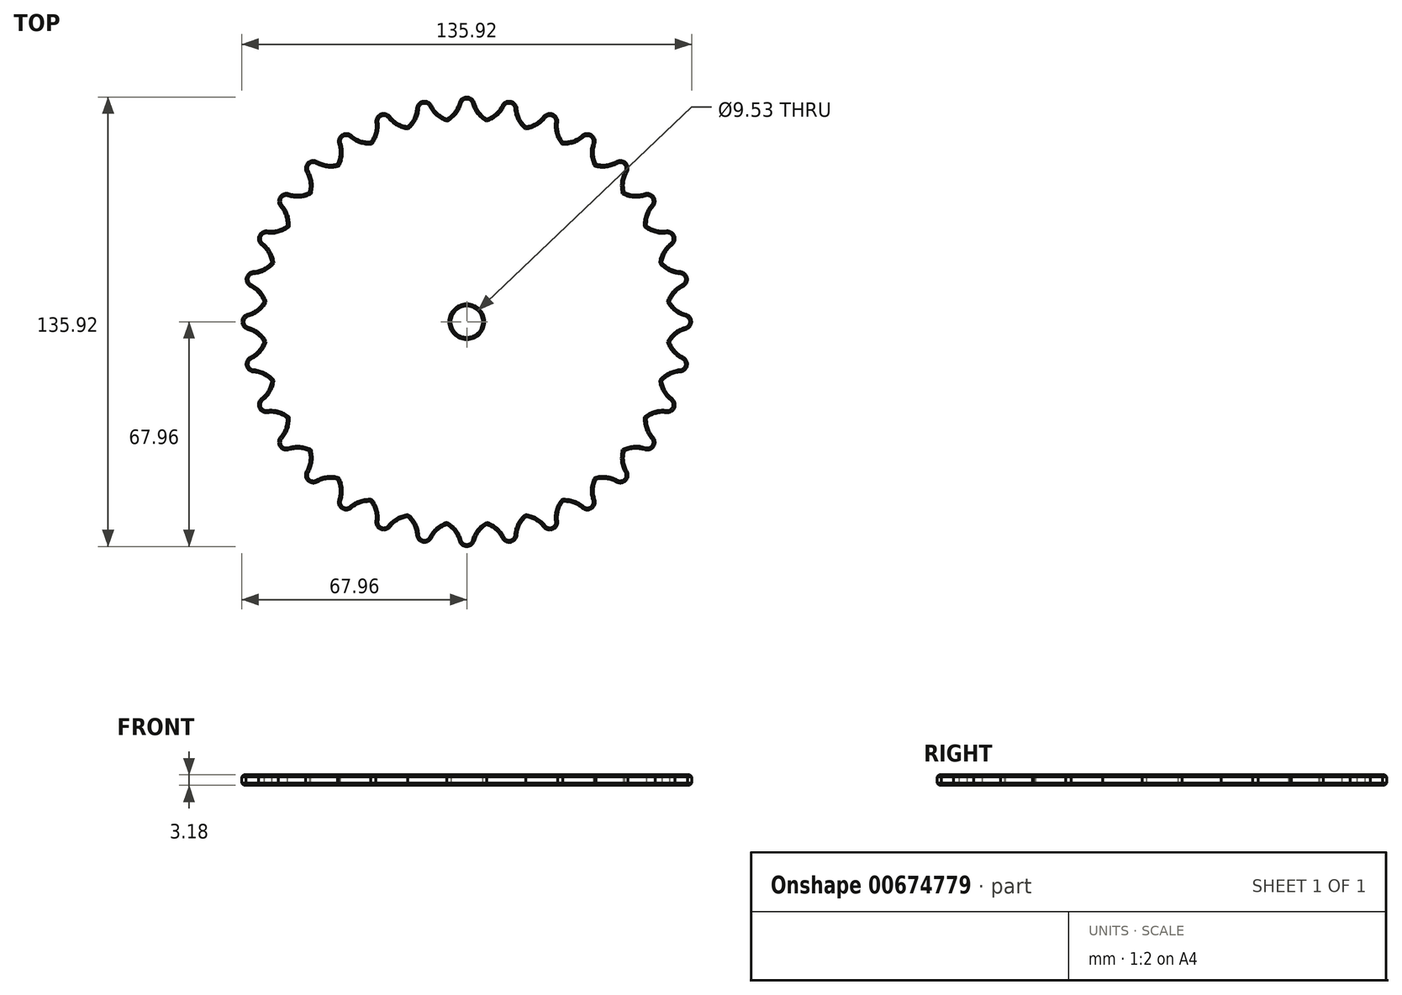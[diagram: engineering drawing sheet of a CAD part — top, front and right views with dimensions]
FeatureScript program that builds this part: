
annotation { "Feature Type Name" : "Feature", "Feature Type Description" : "" }
export const myFeature = defineFeature(function(context is Context, id is Id, definition is map)
    precondition{}
    {
        {
            var Q0;
            Q0=qCreatedBy(makeId("Top.planeOp"),FACE);
            var sketch = newSketch(context, id + "F0", { "sketchPlane" : qUnion([Q0])});
            skCircle(sketch, "E0", {"center": v(0, 0) * mm, "radius": 64.79 * mm, "construction": true});
            skCircle(sketch, "E1.0", {"center": v(0, 0) * mm, "radius": 67.96 * mm});
            skCircle(sketch, "E2.0", {"center": v(0, 0) * mm, "radius": 61.61 * mm, "construction": true});
            skCircle(sketch, "E3", {"center": v(0, 0) * mm, "radius": 4.76 * mm});
            skLineSegment(sketch, "E4", {"start": v(0, 0) * mm, "end": v(0, 67.96) * mm});
            skLineSegment(sketch, "E5", {"start": v(0, 0) * mm, "end": v(6.04, 61.31) * mm});
            skCircle(sketch, "E6", {"center": v(0, 67.96) * mm, "radius": 2.38 * mm});
            skLineSegment(sketch, "E7", {"start": v(0, 67.96) * mm, "end": v(2.94, 69.66) * mm});
            skLineSegment(sketch, "E8", {"start": v(0, 67.96) * mm, "end": v(2.38, 67.96) * mm});
            skArc(sketch, "E9", {"start": v(2.3, 66.2) * mm, "mid": v(0, 67.96) * mm, "end": v(-2.3, 66.2) * mm});
            skLineSegment(sketch, "E10", {"start": v(0, 65.58) * mm, "end": v(2.38, 65.58) * mm});
            skLineSegment(sketch, "E11", {"start": v(0, 65.58) * mm, "end": v(3.51, 66.52) * mm});
            skLineSegment(sketch, "E12.MirrorCS", {"start": v(0, 65.58) * mm, "end": v(-3.51, 66.52) * mm});
            skLineSegment(sketch, "E13", {"start": v(2.3, 66.2) * mm, "end": v(2.97, 63.7) * mm});
            skLineSegment(sketch, "E14", {"start": v(-2.3, 66.2) * mm, "end": v(-3.02, 63.53) * mm});
            skArc(sketch, "E15.1.0", {"start": v(-10.66, 65.37) * mm, "mid": v(-13.26, 66.66) * mm, "end": v(-15.17, 64.48) * mm});
            skArc(sketch, "E15.2.0", {"start": v(-23.2, 62.04) * mm, "mid": v(-26, 62.79) * mm, "end": v(-27.46, 60.28) * mm});
            skArc(sketch, "E15.3.0", {"start": v(-34.86, 56.32) * mm, "mid": v(-37.76, 56.5) * mm, "end": v(-38.69, 53.76) * mm});
            skArc(sketch, "E15.4.0", {"start": v(-45.18, 48.43) * mm, "mid": v(-48.06, 48.06) * mm, "end": v(-48.43, 45.18) * mm});
            skArc(sketch, "E15.5.0", {"start": v(-53.76, 38.69) * mm, "mid": v(-56.5, 37.76) * mm, "end": v(-56.32, 34.86) * mm});
            skArc(sketch, "E15.6.0", {"start": v(-60.28, 27.46) * mm, "mid": v(-62.79, 26) * mm, "end": v(-62.04, 23.2) * mm});
            skArc(sketch, "E15.7.0", {"start": v(-64.48, 15.17) * mm, "mid": v(-66.66, 13.26) * mm, "end": v(-65.37, 10.66) * mm});
            skArc(sketch, "E15.8.0", {"start": v(-66.2, 2.3) * mm, "mid": v(-67.96, 0) * mm, "end": v(-66.2, -2.3) * mm});
            skArc(sketch, "E15.9.0", {"start": v(-65.37, -10.66) * mm, "mid": v(-66.66, -13.26) * mm, "end": v(-64.48, -15.17) * mm});
            skArc(sketch, "E15.10.0", {"start": v(-62.04, -23.2) * mm, "mid": v(-62.79, -26) * mm, "end": v(-60.28, -27.46) * mm});
            skArc(sketch, "E15.11.0", {"start": v(-56.32, -34.86) * mm, "mid": v(-56.5, -37.76) * mm, "end": v(-53.76, -38.69) * mm});
            skArc(sketch, "E15.12.0", {"start": v(-48.43, -45.18) * mm, "mid": v(-48.06, -48.06) * mm, "end": v(-45.18, -48.43) * mm});
            skArc(sketch, "E15.13.0", {"start": v(-38.69, -53.76) * mm, "mid": v(-37.76, -56.5) * mm, "end": v(-34.86, -56.32) * mm});
            skArc(sketch, "E15.14.0", {"start": v(-27.46, -60.28) * mm, "mid": v(-26, -62.79) * mm, "end": v(-23.2, -62.04) * mm});
            skArc(sketch, "E15.15.0", {"start": v(-15.17, -64.48) * mm, "mid": v(-13.26, -66.66) * mm, "end": v(-10.66, -65.37) * mm});
            skArc(sketch, "E15.16.0", {"start": v(-2.3, -66.2) * mm, "mid": v(0, -67.96) * mm, "end": v(2.3, -66.2) * mm});
            skArc(sketch, "E15.17.0", {"start": v(10.66, -65.37) * mm, "mid": v(13.26, -66.66) * mm, "end": v(15.17, -64.48) * mm});
            skArc(sketch, "E15.18.0", {"start": v(23.2, -62.04) * mm, "mid": v(26, -62.79) * mm, "end": v(27.46, -60.28) * mm});
            skArc(sketch, "E15.19.0", {"start": v(34.86, -56.32) * mm, "mid": v(37.76, -56.5) * mm, "end": v(38.69, -53.76) * mm});
            skArc(sketch, "E15.20.0", {"start": v(45.18, -48.43) * mm, "mid": v(48.06, -48.06) * mm, "end": v(48.43, -45.18) * mm});
            skArc(sketch, "E15.21.0", {"start": v(53.76, -38.69) * mm, "mid": v(56.5, -37.76) * mm, "end": v(56.32, -34.86) * mm});
            skArc(sketch, "E15.22.0", {"start": v(60.28, -27.46) * mm, "mid": v(62.79, -26) * mm, "end": v(62.04, -23.2) * mm});
            skArc(sketch, "E15.23.0", {"start": v(64.48, -15.17) * mm, "mid": v(66.66, -13.26) * mm, "end": v(65.37, -10.66) * mm});
            skArc(sketch, "E15.24.0", {"start": v(66.2, -2.3) * mm, "mid": v(67.96, 0) * mm, "end": v(66.2, 2.3) * mm});
            skArc(sketch, "E15.25.0", {"start": v(65.37, 10.66) * mm, "mid": v(66.66, 13.26) * mm, "end": v(64.48, 15.17) * mm});
            skArc(sketch, "E15.26.0", {"start": v(62.04, 23.2) * mm, "mid": v(62.79, 26) * mm, "end": v(60.28, 27.46) * mm});
            skArc(sketch, "E15.27.0", {"start": v(56.32, 34.86) * mm, "mid": v(56.5, 37.76) * mm, "end": v(53.76, 38.69) * mm});
            skArc(sketch, "E15.28.0", {"start": v(48.43, 45.18) * mm, "mid": v(48.06, 48.06) * mm, "end": v(45.18, 48.43) * mm});
            skArc(sketch, "E15.29.0", {"start": v(38.69, 53.76) * mm, "mid": v(37.76, 56.5) * mm, "end": v(34.86, 56.32) * mm});
            skArc(sketch, "E15.30.0", {"start": v(27.46, 60.28) * mm, "mid": v(26, 62.79) * mm, "end": v(23.2, 62.04) * mm});
            skArc(sketch, "E15.31.0", {"start": v(15.17, 64.48) * mm, "mid": v(13.26, 66.66) * mm, "end": v(10.66, 65.37) * mm});
            skArc(sketch, "E16", {"start": v(2.3, 66.2) * mm, "mid": v(3.69, 63.38) * mm, "end": v(6.04, 61.31) * mm});
            skLineSegment(sketch, "E17.MirrorCS", {"start": v(0, 0) * mm, "end": v(-6.04, 61.31) * mm});
            skArc(sketch, "E18", {"start": v(-6.04, 61.31) * mm, "mid": v(-3.69, 63.38) * mm, "end": v(-2.3, 66.2) * mm});
            skArc(sketch, "E19.1.0", {"start": v(-10.66, 65.37) * mm, "mid": v(-8.75, 62.89) * mm, "end": v(-6.04, 61.31) * mm});
            skArc(sketch, "E19.1.1", {"start": v(-17.88, 58.96) * mm, "mid": v(-15.98, 61.45) * mm, "end": v(-15.17, 64.48) * mm});
            skArc(sketch, "E19.2.0", {"start": v(-23.2, 62.04) * mm, "mid": v(-20.85, 59.97) * mm, "end": v(-17.88, 58.96) * mm});
            skArc(sketch, "E19.2.1", {"start": v(-29.04, 54.34) * mm, "mid": v(-27.66, 57.15) * mm, "end": v(-27.46, 60.28) * mm});
            skArc(sketch, "E19.3.0", {"start": v(-34.86, 56.32) * mm, "mid": v(-32.15, 54.75) * mm, "end": v(-29.04, 54.34) * mm});
            skArc(sketch, "E19.3.1", {"start": v(-39.09, 47.63) * mm, "mid": v(-38.28, 50.65) * mm, "end": v(-38.69, 53.76) * mm});
            skArc(sketch, "E19.4.0", {"start": v(-45.18, 48.43) * mm, "mid": v(-42.21, 47.43) * mm, "end": v(-39.09, 47.63) * mm});
            skArc(sketch, "E19.4.1", {"start": v(-47.63, 39.09) * mm, "mid": v(-47.43, 42.21) * mm, "end": v(-48.43, 45.18) * mm});
            skArc(sketch, "E19.5.0", {"start": v(-53.76, 38.69) * mm, "mid": v(-50.65, 38.28) * mm, "end": v(-47.63, 39.09) * mm});
            skArc(sketch, "E19.5.1", {"start": v(-54.34, 29.04) * mm, "mid": v(-54.75, 32.15) * mm, "end": v(-56.32, 34.86) * mm});
            skArc(sketch, "E19.6.0", {"start": v(-60.28, 27.46) * mm, "mid": v(-57.15, 27.66) * mm, "end": v(-54.34, 29.04) * mm});
            skArc(sketch, "E19.6.1", {"start": v(-58.96, 17.88) * mm, "mid": v(-59.97, 20.85) * mm, "end": v(-62.04, 23.2) * mm});
            skArc(sketch, "E19.7.0", {"start": v(-64.48, 15.17) * mm, "mid": v(-61.45, 15.98) * mm, "end": v(-58.96, 17.88) * mm});
            skArc(sketch, "E19.7.1", {"start": v(-61.31, 6.04) * mm, "mid": v(-62.89, 8.75) * mm, "end": v(-65.37, 10.66) * mm});
            skArc(sketch, "E19.8.0", {"start": v(-66.2, 2.3) * mm, "mid": v(-63.38, 3.69) * mm, "end": v(-61.31, 6.04) * mm});
            skArc(sketch, "E19.8.1", {"start": v(-61.31, -6.04) * mm, "mid": v(-63.38, -3.69) * mm, "end": v(-66.2, -2.3) * mm});
            skArc(sketch, "E19.9.0", {"start": v(-65.37, -10.66) * mm, "mid": v(-62.89, -8.75) * mm, "end": v(-61.31, -6.04) * mm});
            skArc(sketch, "E19.9.1", {"start": v(-58.96, -17.88) * mm, "mid": v(-61.45, -15.98) * mm, "end": v(-64.48, -15.17) * mm});
            skArc(sketch, "E19.10.0", {"start": v(-62.04, -23.2) * mm, "mid": v(-59.97, -20.85) * mm, "end": v(-58.96, -17.88) * mm});
            skArc(sketch, "E19.10.1", {"start": v(-54.34, -29.04) * mm, "mid": v(-57.15, -27.66) * mm, "end": v(-60.28, -27.46) * mm});
            skArc(sketch, "E19.11.0", {"start": v(-56.32, -34.86) * mm, "mid": v(-54.75, -32.15) * mm, "end": v(-54.34, -29.04) * mm});
            skArc(sketch, "E19.11.1", {"start": v(-47.63, -39.09) * mm, "mid": v(-50.65, -38.28) * mm, "end": v(-53.76, -38.69) * mm});
            skArc(sketch, "E19.12.0", {"start": v(-48.43, -45.18) * mm, "mid": v(-47.43, -42.21) * mm, "end": v(-47.63, -39.09) * mm});
            skArc(sketch, "E19.12.1", {"start": v(-39.09, -47.63) * mm, "mid": v(-42.21, -47.43) * mm, "end": v(-45.18, -48.43) * mm});
            skArc(sketch, "E19.13.0", {"start": v(-38.69, -53.76) * mm, "mid": v(-38.28, -50.65) * mm, "end": v(-39.09, -47.63) * mm});
            skArc(sketch, "E19.13.1", {"start": v(-29.04, -54.34) * mm, "mid": v(-32.15, -54.75) * mm, "end": v(-34.86, -56.32) * mm});
            skArc(sketch, "E19.14.0", {"start": v(-27.46, -60.28) * mm, "mid": v(-27.66, -57.15) * mm, "end": v(-29.04, -54.34) * mm});
            skArc(sketch, "E19.14.1", {"start": v(-17.88, -58.96) * mm, "mid": v(-20.85, -59.97) * mm, "end": v(-23.2, -62.04) * mm});
            skArc(sketch, "E19.15.0", {"start": v(-15.17, -64.48) * mm, "mid": v(-15.98, -61.45) * mm, "end": v(-17.88, -58.96) * mm});
            skArc(sketch, "E19.15.1", {"start": v(-6.04, -61.31) * mm, "mid": v(-8.75, -62.89) * mm, "end": v(-10.66, -65.37) * mm});
            skArc(sketch, "E19.16.0", {"start": v(-2.3, -66.2) * mm, "mid": v(-3.69, -63.38) * mm, "end": v(-6.04, -61.31) * mm});
            skArc(sketch, "E19.16.1", {"start": v(6.04, -61.31) * mm, "mid": v(3.69, -63.38) * mm, "end": v(2.3, -66.2) * mm});
            skArc(sketch, "E19.17.0", {"start": v(10.66, -65.37) * mm, "mid": v(8.75, -62.89) * mm, "end": v(6.04, -61.31) * mm});
            skArc(sketch, "E19.17.1", {"start": v(17.88, -58.96) * mm, "mid": v(15.98, -61.45) * mm, "end": v(15.17, -64.48) * mm});
            skArc(sketch, "E19.18.0", {"start": v(23.2, -62.04) * mm, "mid": v(20.85, -59.97) * mm, "end": v(17.88, -58.96) * mm});
            skArc(sketch, "E19.18.1", {"start": v(29.04, -54.34) * mm, "mid": v(27.66, -57.15) * mm, "end": v(27.46, -60.28) * mm});
            skArc(sketch, "E19.19.0", {"start": v(34.86, -56.32) * mm, "mid": v(32.15, -54.75) * mm, "end": v(29.04, -54.34) * mm});
            skArc(sketch, "E19.19.1", {"start": v(39.09, -47.63) * mm, "mid": v(38.28, -50.65) * mm, "end": v(38.69, -53.76) * mm});
            skArc(sketch, "E19.20.0", {"start": v(45.18, -48.43) * mm, "mid": v(42.21, -47.43) * mm, "end": v(39.09, -47.63) * mm});
            skArc(sketch, "E19.20.1", {"start": v(47.63, -39.09) * mm, "mid": v(47.43, -42.21) * mm, "end": v(48.43, -45.18) * mm});
            skArc(sketch, "E19.21.0", {"start": v(53.76, -38.69) * mm, "mid": v(50.65, -38.28) * mm, "end": v(47.63, -39.09) * mm});
            skArc(sketch, "E19.21.1", {"start": v(54.34, -29.04) * mm, "mid": v(54.75, -32.15) * mm, "end": v(56.32, -34.86) * mm});
            skArc(sketch, "E19.22.0", {"start": v(60.28, -27.46) * mm, "mid": v(57.15, -27.66) * mm, "end": v(54.34, -29.04) * mm});
            skArc(sketch, "E19.22.1", {"start": v(58.96, -17.88) * mm, "mid": v(59.97, -20.85) * mm, "end": v(62.04, -23.2) * mm});
            skArc(sketch, "E19.23.0", {"start": v(64.48, -15.17) * mm, "mid": v(61.45, -15.98) * mm, "end": v(58.96, -17.88) * mm});
            skArc(sketch, "E19.23.1", {"start": v(61.31, -6.04) * mm, "mid": v(62.89, -8.75) * mm, "end": v(65.37, -10.66) * mm});
            skArc(sketch, "E19.24.0", {"start": v(66.2, -2.3) * mm, "mid": v(63.38, -3.69) * mm, "end": v(61.31, -6.04) * mm});
            skArc(sketch, "E19.24.1", {"start": v(61.31, 6.04) * mm, "mid": v(63.38, 3.69) * mm, "end": v(66.2, 2.3) * mm});
            skArc(sketch, "E19.25.0", {"start": v(65.37, 10.66) * mm, "mid": v(62.89, 8.75) * mm, "end": v(61.31, 6.04) * mm});
            skArc(sketch, "E19.25.1", {"start": v(58.96, 17.88) * mm, "mid": v(61.45, 15.98) * mm, "end": v(64.48, 15.17) * mm});
            skArc(sketch, "E19.26.0", {"start": v(62.04, 23.2) * mm, "mid": v(59.97, 20.85) * mm, "end": v(58.96, 17.88) * mm});
            skArc(sketch, "E19.26.1", {"start": v(54.34, 29.04) * mm, "mid": v(57.15, 27.66) * mm, "end": v(60.28, 27.46) * mm});
            skArc(sketch, "E19.27.0", {"start": v(56.32, 34.86) * mm, "mid": v(54.75, 32.15) * mm, "end": v(54.34, 29.04) * mm});
            skArc(sketch, "E19.27.1", {"start": v(47.63, 39.09) * mm, "mid": v(50.65, 38.28) * mm, "end": v(53.76, 38.69) * mm});
            skArc(sketch, "E19.28.0", {"start": v(48.43, 45.18) * mm, "mid": v(47.43, 42.21) * mm, "end": v(47.63, 39.09) * mm});
            skArc(sketch, "E19.28.1", {"start": v(39.09, 47.63) * mm, "mid": v(42.21, 47.43) * mm, "end": v(45.18, 48.43) * mm});
            skArc(sketch, "E19.29.0", {"start": v(38.69, 53.76) * mm, "mid": v(38.28, 50.65) * mm, "end": v(39.09, 47.63) * mm});
            skArc(sketch, "E19.29.1", {"start": v(29.04, 54.34) * mm, "mid": v(32.15, 54.75) * mm, "end": v(34.86, 56.32) * mm});
            skArc(sketch, "E19.30.0", {"start": v(27.46, 60.28) * mm, "mid": v(27.66, 57.15) * mm, "end": v(29.04, 54.34) * mm});
            skArc(sketch, "E19.30.1", {"start": v(17.88, 58.96) * mm, "mid": v(20.85, 59.97) * mm, "end": v(23.2, 62.04) * mm});
            skArc(sketch, "E19.31.0", {"start": v(15.17, 64.48) * mm, "mid": v(15.98, 61.45) * mm, "end": v(17.88, 58.96) * mm});
            skArc(sketch, "E19.31.1", {"start": v(6.04, 61.31) * mm, "mid": v(8.75, 62.89) * mm, "end": v(10.66, 65.37) * mm});
            skPoint(sketch, "E20", {"position": v(-27.4, 58.7) * mm});
            skPoint(sketch, "E21", {"position": v(-15.43, 62.92) * mm});
            skSolve(sketch);
        }
        {
            var Q0;
            {var subQ28=sQuery(id+"F0.wireOp",EDGE,"E19.1.0");Q0=makeQuery(id+"F0.imprint","IMPRINT",FACE,{"disambiguationData":[TD([[makeQuery(id+"F0.imprint","IMPRINT",EDGE,{"derivedFrom":subQ28}),-1.0]])]});}
            var Q1;
            {var subQ5=sQuery(id+"F0.wireOp",EDGE,"E16");Q1=makeQuery(id+"F0.imprint","IMPRINT",FACE,{"disambiguationData":[TD([[makeQuery(id+"F0.imprint","IMPRINT",EDGE,{"derivedFrom":subQ5}),-1.0]])]});}
            var Q2;
            {var subQ9=sQuery(id+"F0.wireOp",EDGE,"E18");Q2=makeQuery(id+"F0.imprint","IMPRINT",FACE,{"disambiguationData":[TD([[makeQuery(id+"F0.imprint","IMPRINT",EDGE,{"derivedFrom":subQ9}),-1.0]])]});}
            var Q3;
            {var subQ3=sQuery(id+"F0.wireOp",EDGE,"E11");var subQ4=sQuery(id+"F0.wireOp",EDGE,"E6");var subQ7=makeQuery(id+"F0.imprint","INTERSECT",VERTEX,{"derivedFrom":[subQ4,subQ3]});Q3=makeQuery(id+"F0.imprint","IMPRINT",FACE,{"disambiguationData":[TD([[makeQuery(id+"F0.imprint","IMPRINT",EDGE,{"disambiguationData":[TD([[subQ7,-1.0]])],"derivedFrom":subQ4}),1.0]])]});}
            var Q4;
            {var subQ0=sQuery(id+"F0.wireOp",EDGE,"E11");var subQ1=sQuery(id+"F0.wireOp",EDGE,"E6");var subQ2=makeQuery(id+"F0.imprint","INTERSECT",VERTEX,{"derivedFrom":[subQ1,subQ0]});Q4=makeQuery(id+"F0.imprint","IMPRINT",FACE,{"disambiguationData":[TD([[makeQuery(id+"F0.imprint","IMPRINT",EDGE,{"disambiguationData":[TD([[subQ2,-1.0]])],"derivedFrom":subQ1}),-1.0]])]});}
            var Q5;
            {var subQ0=sQuery(id+"F0.wireOp",EDGE,"E11");var subQ1=sQuery(id+"F0.wireOp",EDGE,"E6");var subQ3=makeQuery(id+"F0.imprint","INTERSECT",VERTEX,{"derivedFrom":[subQ1,subQ0]});Q5=makeQuery(id+"F0.imprint","IMPRINT",FACE,{"disambiguationData":[TD([[makeQuery(id+"F0.imprint","IMPRINT",EDGE,{"disambiguationData":[TD([[subQ3,1.0]])],"derivedFrom":subQ1}),1.0]])]});}
            var Q6;
            {var subQ0=sQuery(id+"F0.wireOp",EDGE,"E12.MirrorCS");var subQ1=sQuery(id+"F0.wireOp",EDGE,"E6");var subQ3=makeQuery(id+"F0.imprint","INTERSECT",VERTEX,{"derivedFrom":[subQ1,subQ0]});Q6=makeQuery(id+"F0.imprint","IMPRINT",FACE,{"disambiguationData":[TD([[makeQuery(id+"F0.imprint","IMPRINT",EDGE,{"disambiguationData":[TD([[subQ3,-1.0]])],"derivedFrom":subQ1}),1.0]])]});}
            var Q7;
            {var subQ0=sQuery(id+"F0.wireOp",EDGE,"E9");var subQ4=sQuery(id+"F0.wireOp",EDGE,"E6");var subQ7=makeQuery(id+"F0.imprint","INTERSECT",VERTEX,{"disambiguationData":[OD(0.0)],"derivedFrom":[subQ4,subQ0]});Q7=makeQuery(id+"F0.imprint","IMPRINT",FACE,{"disambiguationData":[TD([[makeQuery(id+"F0.imprint","IMPRINT",EDGE,{"disambiguationData":[TD([[subQ7,-1.0]])],"derivedFrom":subQ4}),1.0]])]});}
            var Q8;
            {var subQ0=sQuery(id+"F0.wireOp",EDGE,"E9");var subQ1=sQuery(id+"F0.wireOp",EDGE,"E6");var subQ2=makeQuery(id+"F0.imprint","INTERSECT",VERTEX,{"disambiguationData":[OD(0.0)],"derivedFrom":[subQ1,subQ0]});Q8=makeQuery(id+"F0.imprint","IMPRINT",FACE,{"disambiguationData":[TD([[makeQuery(id+"F0.imprint","IMPRINT",EDGE,{"disambiguationData":[TD([[subQ2,-1.0]])],"derivedFrom":subQ1}),-1.0]])]});}
            extrude(context, id + "F1", {"entities" : qUnion([Q0, Q1, Q2, Q3, Q4, Q5, Q6, Q7, Q8]), "depth" : 3.17 * mm, "offsetDistance" : 25.4 * mm});
        }
        {
            var Q0;
            Q0=makeQuery(id+"F1.opExtrude","CAP_FACE",FACE,{"disambiguationData":[OSD([sQuery(id+"F0.wireOp",EDGE,"E3"),sQuery(id+"F0.wireOp",EDGE,"E9"),sQuery(id+"F0.wireOp",EDGE,"E15.1.0"),sQuery(id+"F0.wireOp",EDGE,"E15.2.0"),sQuery(id+"F0.wireOp",EDGE,"E15.3.0"),sQuery(id+"F0.wireOp",EDGE,"E15.4.0"),sQuery(id+"F0.wireOp",EDGE,"E15.5.0"),sQuery(id+"F0.wireOp",EDGE,"E15.6.0"),sQuery(id+"F0.wireOp",EDGE,"E15.7.0"),sQuery(id+"F0.wireOp",EDGE,"E15.8.0"),sQuery(id+"F0.wireOp",EDGE,"E15.9.0"),sQuery(id+"F0.wireOp",EDGE,"E15.10.0"),sQuery(id+"F0.wireOp",EDGE,"E15.11.0"),sQuery(id+"F0.wireOp",EDGE,"E15.12.0"),sQuery(id+"F0.wireOp",EDGE,"E15.13.0"),sQuery(id+"F0.wireOp",EDGE,"E15.14.0"),sQuery(id+"F0.wireOp",EDGE,"E15.15.0"),sQuery(id+"F0.wireOp",EDGE,"E15.16.0"),sQuery(id+"F0.wireOp",EDGE,"E15.17.0"),sQuery(id+"F0.wireOp",EDGE,"E15.18.0"),sQuery(id+"F0.wireOp",EDGE,"E15.19.0"),sQuery(id+"F0.wireOp",EDGE,"E15.20.0"),sQuery(id+"F0.wireOp",EDGE,"E15.21.0"),sQuery(id+"F0.wireOp",EDGE,"E15.22.0"),sQuery(id+"F0.wireOp",EDGE,"E15.23.0"),sQuery(id+"F0.wireOp",EDGE,"E15.24.0"),sQuery(id+"F0.wireOp",EDGE,"E15.25.0"),sQuery(id+"F0.wireOp",EDGE,"E15.26.0"),sQuery(id+"F0.wireOp",EDGE,"E15.27.0"),sQuery(id+"F0.wireOp",EDGE,"E15.28.0"),sQuery(id+"F0.wireOp",EDGE,"E15.29.0"),sQuery(id+"F0.wireOp",EDGE,"E15.30.0"),sQuery(id+"F0.wireOp",EDGE,"E15.31.0"),sQuery(id+"F0.wireOp",EDGE,"E16"),sQuery(id+"F0.wireOp",EDGE,"E18"),sQuery(id+"F0.wireOp",EDGE,"E19.1.0"),sQuery(id+"F0.wireOp",EDGE,"E19.1.1"),sQuery(id+"F0.wireOp",EDGE,"E19.2.0"),sQuery(id+"F0.wireOp",EDGE,"E19.2.1"),sQuery(id+"F0.wireOp",EDGE,"E19.3.0"),sQuery(id+"F0.wireOp",EDGE,"E19.3.1"),sQuery(id+"F0.wireOp",EDGE,"E19.4.0"),sQuery(id+"F0.wireOp",EDGE,"E19.4.1"),sQuery(id+"F0.wireOp",EDGE,"E19.5.0"),sQuery(id+"F0.wireOp",EDGE,"E19.5.1"),sQuery(id+"F0.wireOp",EDGE,"E19.6.0"),sQuery(id+"F0.wireOp",EDGE,"E19.6.1"),sQuery(id+"F0.wireOp",EDGE,"E19.7.0"),sQuery(id+"F0.wireOp",EDGE,"E19.7.1"),sQuery(id+"F0.wireOp",EDGE,"E19.8.0"),sQuery(id+"F0.wireOp",EDGE,"E19.8.1"),sQuery(id+"F0.wireOp",EDGE,"E19.9.0"),sQuery(id+"F0.wireOp",EDGE,"E19.9.1"),sQuery(id+"F0.wireOp",EDGE,"E19.10.0"),sQuery(id+"F0.wireOp",EDGE,"E19.10.1"),sQuery(id+"F0.wireOp",EDGE,"E19.11.0"),sQuery(id+"F0.wireOp",EDGE,"E19.11.1"),sQuery(id+"F0.wireOp",EDGE,"E19.12.0"),sQuery(id+"F0.wireOp",EDGE,"E19.12.1"),sQuery(id+"F0.wireOp",EDGE,"E19.13.0"),sQuery(id+"F0.wireOp",EDGE,"E19.13.1"),sQuery(id+"F0.wireOp",EDGE,"E19.14.0"),sQuery(id+"F0.wireOp",EDGE,"E19.14.1"),sQuery(id+"F0.wireOp",EDGE,"E19.15.0"),sQuery(id+"F0.wireOp",EDGE,"E19.15.1"),sQuery(id+"F0.wireOp",EDGE,"E19.16.0"),sQuery(id+"F0.wireOp",EDGE,"E19.16.1"),sQuery(id+"F0.wireOp",EDGE,"E19.17.0"),sQuery(id+"F0.wireOp",EDGE,"E19.17.1"),sQuery(id+"F0.wireOp",EDGE,"E19.18.0"),sQuery(id+"F0.wireOp",EDGE,"E19.18.1"),sQuery(id+"F0.wireOp",EDGE,"E19.19.0"),sQuery(id+"F0.wireOp",EDGE,"E19.19.1"),sQuery(id+"F0.wireOp",EDGE,"E19.20.0"),sQuery(id+"F0.wireOp",EDGE,"E19.20.1"),sQuery(id+"F0.wireOp",EDGE,"E19.21.0"),sQuery(id+"F0.wireOp",EDGE,"E19.21.1"),sQuery(id+"F0.wireOp",EDGE,"E19.22.0"),sQuery(id+"F0.wireOp",EDGE,"E19.22.1"),sQuery(id+"F0.wireOp",EDGE,"E19.23.0"),sQuery(id+"F0.wireOp",EDGE,"E19.23.1"),sQuery(id+"F0.wireOp",EDGE,"E19.24.0"),sQuery(id+"F0.wireOp",EDGE,"E19.24.1"),sQuery(id+"F0.wireOp",EDGE,"E19.25.0"),sQuery(id+"F0.wireOp",EDGE,"E19.25.1"),sQuery(id+"F0.wireOp",EDGE,"E19.26.0"),sQuery(id+"F0.wireOp",EDGE,"E19.26.1"),sQuery(id+"F0.wireOp",EDGE,"E19.27.0"),sQuery(id+"F0.wireOp",EDGE,"E19.27.1"),sQuery(id+"F0.wireOp",EDGE,"E19.28.0"),sQuery(id+"F0.wireOp",EDGE,"E19.28.1"),sQuery(id+"F0.wireOp",EDGE,"E19.29.0"),sQuery(id+"F0.wireOp",EDGE,"E19.29.1"),sQuery(id+"F0.wireOp",EDGE,"E19.30.0"),sQuery(id+"F0.wireOp",EDGE,"E19.30.1"),sQuery(id+"F0.wireOp",EDGE,"E19.31.0"),sQuery(id+"F0.wireOp",EDGE,"E19.31.1")])],"isStart":false});
            var Q1;
            Q1=makeQuery(id+"F1.opExtrude","CAP_FACE",FACE,{"disambiguationData":[OSD([sQuery(id+"F0.wireOp",EDGE,"E3"),sQuery(id+"F0.wireOp",EDGE,"E9"),sQuery(id+"F0.wireOp",EDGE,"E15.1.0"),sQuery(id+"F0.wireOp",EDGE,"E15.2.0"),sQuery(id+"F0.wireOp",EDGE,"E15.3.0"),sQuery(id+"F0.wireOp",EDGE,"E15.4.0"),sQuery(id+"F0.wireOp",EDGE,"E15.5.0"),sQuery(id+"F0.wireOp",EDGE,"E15.6.0"),sQuery(id+"F0.wireOp",EDGE,"E15.7.0"),sQuery(id+"F0.wireOp",EDGE,"E15.8.0"),sQuery(id+"F0.wireOp",EDGE,"E15.9.0"),sQuery(id+"F0.wireOp",EDGE,"E15.10.0"),sQuery(id+"F0.wireOp",EDGE,"E15.11.0"),sQuery(id+"F0.wireOp",EDGE,"E15.12.0"),sQuery(id+"F0.wireOp",EDGE,"E15.13.0"),sQuery(id+"F0.wireOp",EDGE,"E15.14.0"),sQuery(id+"F0.wireOp",EDGE,"E15.15.0"),sQuery(id+"F0.wireOp",EDGE,"E15.16.0"),sQuery(id+"F0.wireOp",EDGE,"E15.17.0"),sQuery(id+"F0.wireOp",EDGE,"E15.18.0"),sQuery(id+"F0.wireOp",EDGE,"E15.19.0"),sQuery(id+"F0.wireOp",EDGE,"E15.20.0"),sQuery(id+"F0.wireOp",EDGE,"E15.21.0"),sQuery(id+"F0.wireOp",EDGE,"E15.22.0"),sQuery(id+"F0.wireOp",EDGE,"E15.23.0"),sQuery(id+"F0.wireOp",EDGE,"E15.24.0"),sQuery(id+"F0.wireOp",EDGE,"E15.25.0"),sQuery(id+"F0.wireOp",EDGE,"E15.26.0"),sQuery(id+"F0.wireOp",EDGE,"E15.27.0"),sQuery(id+"F0.wireOp",EDGE,"E15.28.0"),sQuery(id+"F0.wireOp",EDGE,"E15.29.0"),sQuery(id+"F0.wireOp",EDGE,"E15.30.0"),sQuery(id+"F0.wireOp",EDGE,"E15.31.0"),sQuery(id+"F0.wireOp",EDGE,"E16"),sQuery(id+"F0.wireOp",EDGE,"E18"),sQuery(id+"F0.wireOp",EDGE,"E19.1.0"),sQuery(id+"F0.wireOp",EDGE,"E19.1.1"),sQuery(id+"F0.wireOp",EDGE,"E19.2.0"),sQuery(id+"F0.wireOp",EDGE,"E19.2.1"),sQuery(id+"F0.wireOp",EDGE,"E19.3.0"),sQuery(id+"F0.wireOp",EDGE,"E19.3.1"),sQuery(id+"F0.wireOp",EDGE,"E19.4.0"),sQuery(id+"F0.wireOp",EDGE,"E19.4.1"),sQuery(id+"F0.wireOp",EDGE,"E19.5.0"),sQuery(id+"F0.wireOp",EDGE,"E19.5.1"),sQuery(id+"F0.wireOp",EDGE,"E19.6.0"),sQuery(id+"F0.wireOp",EDGE,"E19.6.1"),sQuery(id+"F0.wireOp",EDGE,"E19.7.0"),sQuery(id+"F0.wireOp",EDGE,"E19.7.1"),sQuery(id+"F0.wireOp",EDGE,"E19.8.0"),sQuery(id+"F0.wireOp",EDGE,"E19.8.1"),sQuery(id+"F0.wireOp",EDGE,"E19.9.0"),sQuery(id+"F0.wireOp",EDGE,"E19.9.1"),sQuery(id+"F0.wireOp",EDGE,"E19.10.0"),sQuery(id+"F0.wireOp",EDGE,"E19.10.1"),sQuery(id+"F0.wireOp",EDGE,"E19.11.0"),sQuery(id+"F0.wireOp",EDGE,"E19.11.1"),sQuery(id+"F0.wireOp",EDGE,"E19.12.0"),sQuery(id+"F0.wireOp",EDGE,"E19.12.1"),sQuery(id+"F0.wireOp",EDGE,"E19.13.0"),sQuery(id+"F0.wireOp",EDGE,"E19.13.1"),sQuery(id+"F0.wireOp",EDGE,"E19.14.0"),sQuery(id+"F0.wireOp",EDGE,"E19.14.1"),sQuery(id+"F0.wireOp",EDGE,"E19.15.0"),sQuery(id+"F0.wireOp",EDGE,"E19.15.1"),sQuery(id+"F0.wireOp",EDGE,"E19.16.0"),sQuery(id+"F0.wireOp",EDGE,"E19.16.1"),sQuery(id+"F0.wireOp",EDGE,"E19.17.0"),sQuery(id+"F0.wireOp",EDGE,"E19.17.1"),sQuery(id+"F0.wireOp",EDGE,"E19.18.0"),sQuery(id+"F0.wireOp",EDGE,"E19.18.1"),sQuery(id+"F0.wireOp",EDGE,"E19.19.0"),sQuery(id+"F0.wireOp",EDGE,"E19.19.1"),sQuery(id+"F0.wireOp",EDGE,"E19.20.0"),sQuery(id+"F0.wireOp",EDGE,"E19.20.1"),sQuery(id+"F0.wireOp",EDGE,"E19.21.0"),sQuery(id+"F0.wireOp",EDGE,"E19.21.1"),sQuery(id+"F0.wireOp",EDGE,"E19.22.0"),sQuery(id+"F0.wireOp",EDGE,"E19.22.1"),sQuery(id+"F0.wireOp",EDGE,"E19.23.0"),sQuery(id+"F0.wireOp",EDGE,"E19.23.1"),sQuery(id+"F0.wireOp",EDGE,"E19.24.0"),sQuery(id+"F0.wireOp",EDGE,"E19.24.1"),sQuery(id+"F0.wireOp",EDGE,"E19.25.0"),sQuery(id+"F0.wireOp",EDGE,"E19.25.1"),sQuery(id+"F0.wireOp",EDGE,"E19.26.0"),sQuery(id+"F0.wireOp",EDGE,"E19.26.1"),sQuery(id+"F0.wireOp",EDGE,"E19.27.0"),sQuery(id+"F0.wireOp",EDGE,"E19.27.1"),sQuery(id+"F0.wireOp",EDGE,"E19.28.0"),sQuery(id+"F0.wireOp",EDGE,"E19.28.1"),sQuery(id+"F0.wireOp",EDGE,"E19.29.0"),sQuery(id+"F0.wireOp",EDGE,"E19.29.1"),sQuery(id+"F0.wireOp",EDGE,"E19.30.0"),sQuery(id+"F0.wireOp",EDGE,"E19.30.1"),sQuery(id+"F0.wireOp",EDGE,"E19.31.0"),sQuery(id+"F0.wireOp",EDGE,"E19.31.1")])],"isStart":true});
            chamfer(context, id + "F2", {"entities" : qUnion([Q0, Q1]), "width" : 0.64 * mm, "tangentPropagation" : true});
        }
    });
